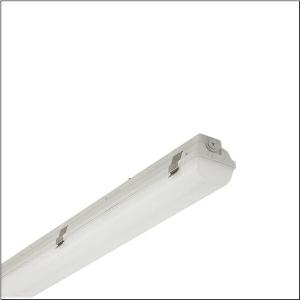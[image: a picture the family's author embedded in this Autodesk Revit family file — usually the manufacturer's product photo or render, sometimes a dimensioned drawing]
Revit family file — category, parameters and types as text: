
# Revit family: monsun_r__21_eco_51fj20dl45a_bcca
name_source: partatom
category: Lighting Fixtures
units: mm (PartAtom-declared; Revit-internal decimal feet)

## family parameters
Cut with Voids When Loaded = No
Host = Face
Light Source = No
Part Type = Normal
Room Calculation Point = No
Round Connector Dimension = Use Diameter
Shared = No

## types (1)
- Monsun® 21 Eco (1 x LED, 4900 lm, 36 W, 4000K)
    Apparent Load = 36 VA
    CIE Flux Codes = 40 69 88 88 100
    Color Rendering = 80
    Color Temperature = 4000K
    Default Elevation = 1800 mm
    Description = Monsun® 21 Eco, damp-proof luminaire, primary optical cover: diffuser, of PC, UV-stabilised, frosted, light emission: direct distribution, primary light characteristic: symmetric, installation type: suspended mounting, surface-mounted, LED, rated luminous flux: 4.900lm, luminous efficacy: 132lm/W, light colour: 840, colour temperature: 4000K, control gear: ECG DALI, with terminal, 5-pole, max. 2.5mm², mains connection: 220..240V, AC, 50/60Hz, rated input power: 36W, housing, of glass-fibre reinforced polyester, light grey (RAL 7035), length: 1.277mm, width: 90mm, height: 95mm, clip for enclosure, of spring steel V2A, protection rating (complete): IP66, insulation class (complete): insulation class I (protective earthing), certification: CE, UKCA, protection symbol: D, impact resistance: IK08, permissible operating ambient temperature: -20..+35°C, corresponds to IFS (International Featured Standards) requirements for safety and quality in the food industry, contact your sales advisor before using the luminaires in applications with unclear chemical exposure, large temperature fluctuations or condensation-forming humidity, packaging unit: 1 piece
    Height = 103 mm
    Lamp = 1 x LED
    Lamp Light Flux = 4900 lm
    Lamp Power = 36 W
    Lamp count = 1
    Length = 1277 mm
    Luminous efficacy = 136 lm/W
    Manufacturer = Siteco
    ModVariant = No
    Model = 51FJ20DL45A
    Mounting Place = Ceiling
    Mounting Type = Surface mounted
    Number of Poles = 1
    OnlyDefault = Yes
    Power Factor = 1
    Product Name = Monsun® 21 Eco
    Product group = damp-proof luminaire
    ProductGroupID = 300
    Protection Class = Protection class I
    Protection Degree = IP 66
    RLX_Detail_Level = 1
    RLX_Emergency_Light_Flux = 0 lm
    RLX_Emergency_Type = 0
    RLX_Emergency_Type_DB = No
    RlxData = <blob elided: 33405 chars, md5=7056c2af>
    Socket = socket
    Standby Power = 0 W
    System Light Flux = 4900 lm
    System Power = 36 W
    Type Comments = Product without accessories
    Type Image = l_1007218.jpg
    URL = http://relux.com
    VarID = ---
    Voltage = 0 V
    Weight = 0.00 kg
    Width = 90 mm

## geometry (parser evidence)
native form markers: Blend x4, Sweep x14
no freeform markers — native parametric forms only
